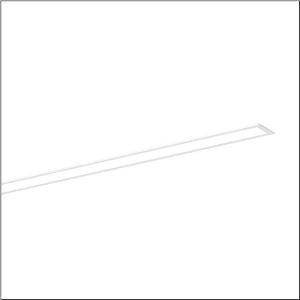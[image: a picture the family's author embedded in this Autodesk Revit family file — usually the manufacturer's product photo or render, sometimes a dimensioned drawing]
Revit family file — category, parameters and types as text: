
# Revit family: silica_r__21_51mx10tbt2w_f160
name_source: partatom
category: Lighting Fixtures
units: mm (PartAtom-declared; Revit-internal decimal feet)

## family parameters
Cut with Voids When Loaded = No
Host = Face
Light Source = No
Part Type = Normal
Room Calculation Point = No
Round Connector Dimension = Use Diameter
Shared = No

## types (1)
- --- (1 x LED, 3000 lm, 25.6 W, 6500K)
    Apparent Load = 26 VA
    CIE Flux Codes = 48 79 96 100 100
    Color Rendering = 80
    Color Temperature = 6500K
    Default Elevation = 1800 mm
    Description = Silica® 21, office luminaire, primary optical cover: cover, of PMMA, opal, light emission: direct distribution, primary light characteristic: symmetric, installation type: recessed, LED, rated luminous flux: 3.000lm, luminous efficacy: 112lm/W, light colour: 8tw, colour temperature: 2700..6500K, control gear: ECG DALI, with terminal, 3+2-pole, max. 2.5mm², mains connection: 220..240V, AC, 50/60Hz, rated input power: 26.9W, luminaire housing, of aluminium, traffic white (RAL 9016), length: 1.504mm, width: 77mm, height: 53mm, protection rating (complete): IP20, insulation class (complete): insulation class I (protective earthing), certification: CE, permissible operating ambient temperature: 0..+35°C, standard: EN 50419, packaging unit: 1 piece
    Height = 0 mm  [stored 0 ft]
    Lamp = 1 x LED
    Lamp Light Flux = 3000 lm
    Lamp Power = 25.6 W
    Lamp count = 1
    Length = 1527 mm
    Luminous efficacy = 117 lm/W
    Manufacturer = Siteco
    ModVariant = No
    Model = 51MX10TBT2W
    Mounting Place = Ceiling
    Mounting Type = Recessed
    Number of Poles = 1
    OnlyDefault = Yes
    Power Factor = 1
    Product Name = Silica® 21
    Product group = office luminaire | ceiling recessed
    ProductGroupID = 401
    Protection Class = Protection class I
    Protection Degree = IP 20
    RLX_Detail_Level = 1
    RLX_Emergency_Light_Flux = 0 lm
    RLX_Emergency_Type = 0
    RLX_Emergency_Type_DB = No
    RlxData = <blob elided: 17885 chars, md5=68b7fd23>
    Socket = socket
    Standby Power = 0 W
    System Light Flux = 3000 lm
    System Power = 26 W
    Type Comments = individual setting
    Type Image = l_1297737.jpg
    URL = http://relux.com
    VarID = @adj_071047
    Voltage = 0 V
    Weight = 0.00 kg
    Width = 79 mm

note: [stored X ft] marks values corroborated as IEEE doubles in the binary element streams (Revit-internal decimal feet)

## geometry (parser evidence)
native form markers: Blend x4, Sweep x11
no freeform markers — native parametric forms only
